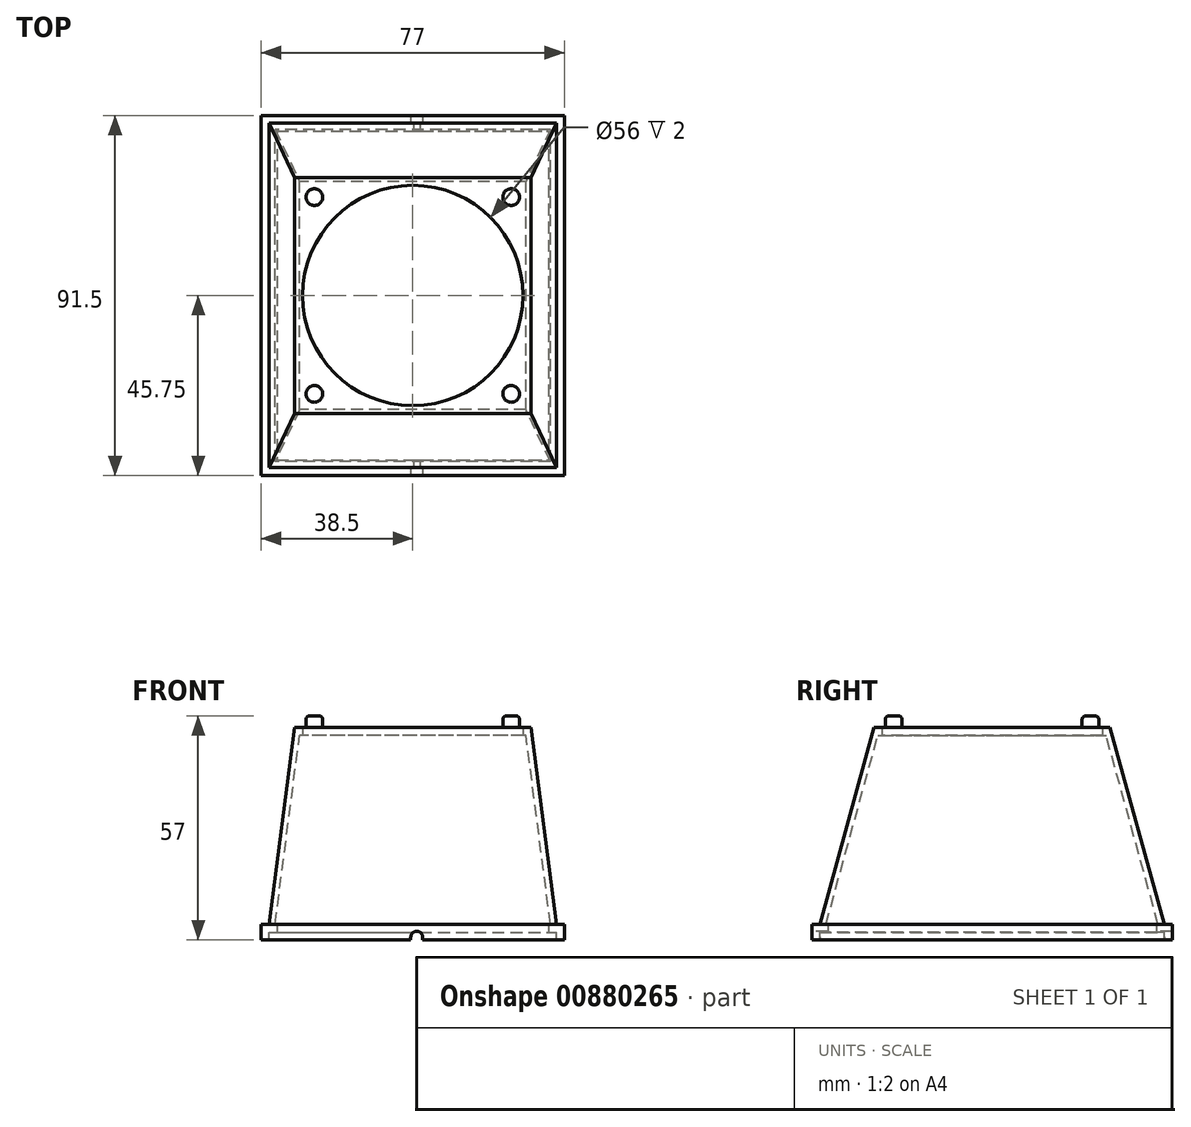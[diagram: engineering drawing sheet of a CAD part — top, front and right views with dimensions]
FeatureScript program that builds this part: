
annotation { "Feature Type Name" : "Feature", "Feature Type Description" : "" }
export const myFeature = defineFeature(function(context is Context, id is Id, definition is map)
    precondition{}
    {
        {
            var Q0;
            Q0=qCreatedBy(makeId("Top.planeOp"),FACE);
            var sketch = newSketch(context, id + "F0", { "sketchPlane" : qUnion([Q0])});
            skCircle(sketch, "E0", {"center": v(0, 0) * mm, "radius": 28 * mm});
            skLineSegment(sketch, "E1.bottom", {"start": v(-30, 30) * mm, "end": v(30, 30) * mm});
            skLineSegment(sketch, "E1.top", {"start": v(-30, -30) * mm, "end": v(30, -30) * mm});
            skLineSegment(sketch, "E1.left", {"start": v(-30, 30) * mm, "end": v(-30, -30) * mm});
            skLineSegment(sketch, "E1.right", {"start": v(30, 30) * mm, "end": v(30, -30) * mm});
            skLineSegment(sketch, "E2.bottom", {"start": v(-34.5, 41.75) * mm, "end": v(34.5, 41.75) * mm});
            skLineSegment(sketch, "E2.top", {"start": v(-34.5, -41.75) * mm, "end": v(34.5, -41.75) * mm});
            skLineSegment(sketch, "E2.left", {"start": v(-34.5, 41.75) * mm, "end": v(-34.5, -41.75) * mm});
            skLineSegment(sketch, "E2.right", {"start": v(34.5, 41.75) * mm, "end": v(34.5, -41.75) * mm});
            skLineSegment(sketch, "E3.bottom", {"start": v(-36.5, -43.75) * mm, "end": v(36.5, -43.75) * mm});
            skLineSegment(sketch, "E3.top", {"start": v(-36.5, 43.75) * mm, "end": v(36.5, 43.75) * mm});
            skLineSegment(sketch, "E3.left", {"start": v(-36.5, -43.75) * mm, "end": v(-36.5, 43.75) * mm});
            skLineSegment(sketch, "E3.right", {"start": v(36.5, -43.75) * mm, "end": v(36.5, 43.75) * mm});
            skLineSegment(sketch, "E4.bottom", {"start": v(-38.5, 45.75) * mm, "end": v(38.5, 45.75) * mm});
            skLineSegment(sketch, "E4.top", {"start": v(-38.5, -45.75) * mm, "end": v(38.5, -45.75) * mm});
            skLineSegment(sketch, "E4.left", {"start": v(-38.5, 45.75) * mm, "end": v(-38.5, -45.75) * mm});
            skLineSegment(sketch, "E4.right", {"start": v(38.5, 45.75) * mm, "end": v(38.5, -45.75) * mm});
            skCircle(sketch, "E5", {"center": v(-25, 25) * mm, "radius": 2.12 * mm});
            skCircle(sketch, "E6.1.0", {"center": v(-25, -25) * mm, "radius": 2.12 * mm});
            skCircle(sketch, "E6.2.0", {"center": v(25, -25) * mm, "radius": 2.12 * mm});
            skCircle(sketch, "E6.3.0", {"center": v(25, 25) * mm, "radius": 2.12 * mm});
            skSolve(sketch);
        }
        {
            var Q0;
            Q0=makeQuery(id+"F0.imprint","IMPRINT",FACE,{"disambiguationData":[TD([[makeQuery(id+"F0.imprint","IMPRINT",EDGE,{"derivedFrom":sQuery(id+"F0.wireOp",EDGE,"E2.bottom")}),1.0]])]});
            extrude(context, id + "F1", {"entities" : qUnion([Q0]), "depth" : 2 * mm, "offsetDistance" : 25 * mm});
        }
        {
            var Q0;
            Q0=makeQuery(id+"F0.imprint","IMPRINT",FACE,{"disambiguationData":[TD([[makeQuery(id+"F0.imprint","IMPRINT",EDGE,{"derivedFrom":sQuery(id+"F0.wireOp",EDGE,"E0")}),-1.0]])]});
            var Q1;
            Q1=makeQuery(id+"F0.imprint","IMPRINT",FACE,{"disambiguationData":[TD([[makeQuery(id+"F0.imprint","IMPRINT",EDGE,{"derivedFrom":sQuery(id+"F0.wireOp",EDGE,"E6.3.0")}),1.0]])]});
            var Q2;
            Q2=makeQuery(id+"F0.imprint","IMPRINT",FACE,{"disambiguationData":[TD([[makeQuery(id+"F0.imprint","IMPRINT",EDGE,{"derivedFrom":sQuery(id+"F0.wireOp",EDGE,"E5")}),1.0]])]});
            var Q3;
            Q3=makeQuery(id+"F0.imprint","IMPRINT",FACE,{"disambiguationData":[TD([[makeQuery(id+"F0.imprint","IMPRINT",EDGE,{"derivedFrom":sQuery(id+"F0.wireOp",EDGE,"E6.1.0")}),1.0]])]});
            var Q4;
            Q4=makeQuery(id+"F0.imprint","IMPRINT",FACE,{"disambiguationData":[TD([[makeQuery(id+"F0.imprint","IMPRINT",EDGE,{"derivedFrom":sQuery(id+"F0.wireOp",EDGE,"E6.2.0")}),1.0]])]});
            extrude(context, id + "F2", {"entities" : qUnion([Q0, Q1, Q2, Q3, Q4]), "operationType" : NewBodyOperationType.ADD, "depth" : 52 * mm, "offsetDistance" : 25 * mm, "hasSecondDirection" : true, "secondDirectionOppositeDirection" : false, "secondDirectionDepth" : 50 * mm});
        }
        {
            var Q0;
            Q0=makeQuery(id+"F2.opExtrude","SWEPT_FACE",FACE,{"disambiguationData":[OSD([sQuery(id+"F0.wireOp",EDGE,"E1.bottom")])]});
            var Q1;
            Q1=makeQuery(id+"F1.opExtrude","SWEPT_FACE",FACE,{"disambiguationData":[OSD([sQuery(id+"F0.wireOp",EDGE,"E3.top")])]});
            loft(context, id + "F3", {"operationType" : NewBodyOperationType.ADD, "sheetProfilesArray" : [{ "sheetProfileEntities" : qUnion([Q0]) }, { "sheetProfileEntities" : qUnion([Q1]) }]});
        }
        {
            var Q0;
            Q0=makeQuery(id+"F2.opExtrude","SWEPT_FACE",FACE,{"disambiguationData":[OSD([sQuery(id+"F0.wireOp",EDGE,"E1.right")])]});
            var Q1;
            Q1=makeQuery(id+"F1.opExtrude","SWEPT_FACE",FACE,{"disambiguationData":[OSD([sQuery(id+"F0.wireOp",EDGE,"E3.right")])]});
            loft(context, id + "F4", {"operationType" : NewBodyOperationType.ADD, "sheetProfilesArray" : [{ "sheetProfileEntities" : qUnion([Q0]) }, { "sheetProfileEntities" : qUnion([Q1]) }]});
        }
        {
            var Q0;
            Q0=makeQuery(id+"F1.opExtrude","SWEPT_FACE",FACE,{"disambiguationData":[OSD([sQuery(id+"F0.wireOp",EDGE,"E3.left")])]});
            var Q1;
            Q1=makeQuery(id+"F2.opExtrude","SWEPT_FACE",FACE,{"disambiguationData":[OSD([sQuery(id+"F0.wireOp",EDGE,"E1.left")])]});
            loft(context, id + "F5", {"operationType" : NewBodyOperationType.ADD, "sheetProfilesArray" : [{ "sheetProfileEntities" : qUnion([Q0]) }, { "sheetProfileEntities" : qUnion([Q1]) }]});
        }
        {
            var Q0;
            Q0=makeQuery(id+"F2.opExtrude","SWEPT_FACE",FACE,{"disambiguationData":[OSD([sQuery(id+"F0.wireOp",EDGE,"E1.top")])]});
            var Q1;
            Q1=makeQuery(id+"F1.opExtrude","SWEPT_FACE",FACE,{"disambiguationData":[OSD([sQuery(id+"F0.wireOp",EDGE,"E3.bottom")])]});
            loft(context, id + "F6", {"operationType" : NewBodyOperationType.ADD, "sheetProfilesArray" : [{ "sheetProfileEntities" : qUnion([Q0]) }, { "sheetProfileEntities" : qUnion([Q1]) }]});
        }
        {
            var Q0;
            Q0=makeQuery(id+"F0.imprint","IMPRINT",FACE,{"disambiguationData":[TD([[makeQuery(id+"F0.imprint","IMPRINT",EDGE,{"derivedFrom":sQuery(id+"F0.wireOp",EDGE,"E3.bottom")}),-1.0]])]});
            extrude(context, id + "F7", {"entities" : qUnion([Q0]), "operationType" : NewBodyOperationType.ADD, "oppositeDirection" : true, "depth" : 2 * mm, "offsetDistance" : 25 * mm, "hasSecondDirection" : true, "secondDirectionOppositeDirection" : false, "secondDirectionDepth" : 2 * mm});
        }
        {
            var Q0;
            Q0=makeQuery(id+"F7.opExtrude","SWEPT_FACE",FACE,{"disambiguationData":[OSD([sQuery(id+"F0.wireOp",EDGE,"E4.top")])]});
            var sketch = newSketch(context, id + "F8", { "sketchPlane" : qUnion([Q0])});
            skArc(sketch, "E7", {"start": v(2.5, -1.25) * mm, "mid": v(1, 0.25) * mm, "end": v(-0.5, -1.25) * mm});
            skLineSegment(sketch, "E8", {"start": v(2.5, -1.25) * mm, "end": v(2.5, -2) * mm});
            skPoint(sketch, "E9.end.orphan", {"position": v(1, -2) * mm});
            skPoint(sketch, "E10.center.orphan", {"position": v(0, -1.25) * mm});
            skPoint(sketch, "E11.start.orphan", {"position": v(-1, -1.25) * mm});
            skLineSegment(sketch, "E12", {"start": v(-0.5, -1.25) * mm, "end": v(-0.5, -2) * mm});
            skSolve(sketch);
        }
        {
            var Q0;
            Q0=makeQuery(id+"F8.imprint","IMPRINT",FACE,{"disambiguationData":[TD([[makeQuery(id+"F8.imprint","IMPRINT",EDGE,{"derivedFrom":sQuery(id+"F8.wireOp",EDGE,"E7")}),1.0]])]});
            extrude(context, id + "F9", {"entities" : qUnion([Q0]), "operationType" : NewBodyOperationType.REMOVE, "endBound" : BoundingType.THROUGH_ALL, "oppositeDirection" : true, "depth" : 25 * mm, "offsetDistance" : 25 * mm});
        }
        {
            var Q0;
            Q0=makeQuery(id+"F0.imprint","IMPRINT",FACE,{"disambiguationData":[TD([[makeQuery(id+"F0.imprint","IMPRINT",EDGE,{"derivedFrom":sQuery(id+"F0.wireOp",EDGE,"E6.3.0")}),1.0]])]});
            var Q1;
            Q1=makeQuery(id+"F0.imprint","IMPRINT",FACE,{"disambiguationData":[TD([[makeQuery(id+"F0.imprint","IMPRINT",EDGE,{"derivedFrom":sQuery(id+"F0.wireOp",EDGE,"E5")}),1.0]])]});
            var Q2;
            Q2=makeQuery(id+"F0.imprint","IMPRINT",FACE,{"disambiguationData":[TD([[makeQuery(id+"F0.imprint","IMPRINT",EDGE,{"derivedFrom":sQuery(id+"F0.wireOp",EDGE,"E6.1.0")}),1.0]])]});
            var Q3;
            Q3=makeQuery(id+"F0.imprint","IMPRINT",FACE,{"disambiguationData":[TD([[makeQuery(id+"F0.imprint","IMPRINT",EDGE,{"derivedFrom":sQuery(id+"F0.wireOp",EDGE,"E6.2.0")}),1.0]])]});
            extrude(context, id + "F10", {"entities" : qUnion([Q0, Q1, Q2, Q3]), "operationType" : NewBodyOperationType.ADD, "depth" : 55 * mm, "offsetDistance" : 25 * mm, "hasSecondDirection" : true, "secondDirectionOppositeDirection" : false, "secondDirectionDepth" : 51 * mm});
        }
        {
            var Q0;
            Q0=makeQuery(id+"F10.opExtrude","CAP_EDGE",EDGE,{"disambiguationData":[OSD([sQuery(id+"F0.wireOp",EDGE,"E6.3.0")])],"isStart":false});
            var Q1;
            Q1=makeQuery(id+"F10.opExtrude","CAP_FACE",FACE,{"disambiguationData":[OSD([sQuery(id+"F0.wireOp",EDGE,"E6.2.0")])],"isStart":false});
            var Q2;
            Q2=makeQuery(id+"F10.opExtrude","CAP_FACE",FACE,{"disambiguationData":[OSD([sQuery(id+"F0.wireOp",EDGE,"E6.1.0")])],"isStart":false});
            var Q3;
            Q3=makeQuery(id+"F10.opExtrude","CAP_EDGE",EDGE,{"disambiguationData":[OSD([sQuery(id+"F0.wireOp",EDGE,"E5")])],"isStart":false});
            var Q4;
            {var subQ0=sQuery(id+"F0.wireOp",EDGE,"E1.right");var subQ1=sQuery(id+"F0.wireOp",EDGE,"E1.bottom");var subQ2=makeQuery(id+"F2.opExtrude","CAP_VERTEX",VERTEX,{"disambiguationData":[OSD([subQ1,subQ0])],"isStart":true});var subQ3=sQuery(id+"F0.wireOp",EDGE,"E1.top");var subQ4=sQuery(id+"F0.wireOp",EDGE,"E3.right");var subQ5=sQuery(id+"F0.wireOp",EDGE,"E3.top");var subQ6=sQuery(id+"F0.wireOp",EDGE,"E3.bottom");Q4=makeQuery(id+"F4.opLoft","SWEPT_FACE",FACE,{"disambiguationData":[OSD([subQ1,subQ3,subQ0,subQ6,subQ5,subQ4]),TDD([makeQuery(id+"F1.opExtrude","CAP_VERTEX",VERTEX,{"disambiguationData":[OSD([subQ6,subQ4])],"isStart":true}),makeQuery(id+"F1.opExtrude","CAP_VERTEX",VERTEX,{"disambiguationData":[OSD([subQ5,subQ4])],"isStart":true}),makeQuery(id+"F1.opExtrude","CAP_EDGE",EDGE,{"disambiguationData":[OSD([subQ4])],"isStart":true}),makeQuery(id+"F2.opExtrude","CAP_VERTEX",VERTEX,{"disambiguationData":[OSD([subQ3,subQ0])],"isStart":true}),makeQuery(id+"F2.opExtrude","CAP_EDGE",EDGE,{"disambiguationData":[OSD([subQ0])],"isStart":true}),makeQuery(id+"F3.boolean.opBoolean","MERGE",VERTEX,{"derivedFrom":[subQ2,makeQuery(id+"F3.opLoft","MID_CAP_VERTEX",VERTEX,{"disambiguationData":[OSD([subQ1,subQ0]),TDD([subQ2])],"capPos":0.0})]})])]});}
            fillet(context, id + "F11", {"entities" : qUnion([Q0, Q1, Q2, Q3, Q4]), "radius" : 1 * mm, "tangentPropagation" : true, "allowEdgeOverflow" : false});
        }
        {
            var Q0;
            {var subQ0=sQuery(id+"F0.wireOp",EDGE,"E1.right");var subQ1=sQuery(id+"F0.wireOp",EDGE,"E1.bottom");var subQ2=makeQuery(id+"F2.opExtrude","CAP_VERTEX",VERTEX,{"disambiguationData":[OSD([subQ1,subQ0])],"isStart":false});var subQ3=sQuery(id+"F0.wireOp",EDGE,"E3.right");var subQ4=sQuery(id+"F0.wireOp",EDGE,"E3.top");var subQ5=makeQuery(id+"F1.opExtrude","CAP_VERTEX",VERTEX,{"disambiguationData":[OSD([subQ4,subQ3])],"isStart":false});var subQ6=sQuery(id+"F0.wireOp",EDGE,"E1.top");var subQ7=sQuery(id+"F0.wireOp",EDGE,"E3.bottom");Q0=makeQuery(id+"F4.opLoft","SWEPT_FACE",FACE,{"disambiguationData":[OSD([subQ1,subQ6,subQ0,subQ7,subQ4,subQ3]),TDD([makeQuery(id+"F1.opExtrude","CAP_VERTEX",VERTEX,{"disambiguationData":[OSD([subQ7,subQ3])],"isStart":false}),makeQuery(id+"F1.opExtrude","CAP_EDGE",EDGE,{"disambiguationData":[OSD([subQ3])],"isStart":false}),makeQuery(id+"F2.opExtrude","CAP_VERTEX",VERTEX,{"disambiguationData":[OSD([subQ6,subQ0])],"isStart":false}),makeQuery(id+"F2.opExtrude","CAP_EDGE",EDGE,{"disambiguationData":[OSD([subQ0])],"isStart":false}),makeQuery(id+"F3.boolean.opBoolean","MERGE",VERTEX,{"derivedFrom":[subQ5,makeQuery(id+"F3.opLoft","MID_CAP_VERTEX",VERTEX,{"disambiguationData":[OSD([subQ4,subQ3]),TDD([subQ5])],"capPos":1.0})]}),makeQuery(id+"F3.boolean.opBoolean","MERGE",VERTEX,{"derivedFrom":[subQ2,makeQuery(id+"F3.opLoft","MID_CAP_VERTEX",VERTEX,{"disambiguationData":[OSD([subQ1,subQ0]),TDD([subQ2])],"capPos":0.0})]})])]});}
            extrude(context, id + "F12", {"entities" : qUnion([Q0]), "operationType" : NewBodyOperationType.ADD, "oppositeDirection" : true, "depth" : 1.5 * mm, "offsetDistance" : 25 * mm});
        }
        {
            var Q0;
            {var subQ0=sQuery(id+"F0.wireOp",EDGE,"E1.left");var subQ1=sQuery(id+"F0.wireOp",EDGE,"E1.top");var subQ2=makeQuery(id+"F2.opExtrude","CAP_VERTEX",VERTEX,{"disambiguationData":[OSD([subQ1,subQ0])],"isStart":false});var subQ3=sQuery(id+"F0.wireOp",EDGE,"E3.left");var subQ4=sQuery(id+"F0.wireOp",EDGE,"E3.bottom");var subQ5=makeQuery(id+"F1.opExtrude","CAP_VERTEX",VERTEX,{"disambiguationData":[OSD([subQ4,subQ3])],"isStart":false});var subQ6=sQuery(id+"F0.wireOp",EDGE,"E1.right");var subQ7=makeQuery(id+"F2.opExtrude","CAP_VERTEX",VERTEX,{"disambiguationData":[OSD([subQ1,subQ6])],"isStart":false});var subQ8=sQuery(id+"F0.wireOp",EDGE,"E3.right");var subQ9=makeQuery(id+"F1.opExtrude","CAP_VERTEX",VERTEX,{"disambiguationData":[OSD([subQ4,subQ8])],"isStart":false});Q0=makeQuery(id+"F6.opLoft","SWEPT_FACE",FACE,{"disambiguationData":[OSD([subQ1,subQ0,subQ6,subQ4,subQ3,subQ8]),TDD([makeQuery(id+"F1.opExtrude","CAP_EDGE",EDGE,{"disambiguationData":[OSD([subQ4])],"isStart":false}),makeQuery(id+"F2.opExtrude","CAP_EDGE",EDGE,{"disambiguationData":[OSD([subQ1])],"isStart":false}),makeQuery(id+"F4.boolean.opBoolean","MERGE",VERTEX,{"derivedFrom":[subQ9,makeQuery(id+"F4.opLoft","MID_CAP_VERTEX",VERTEX,{"disambiguationData":[OSD([subQ4,subQ8]),TDD([subQ9])],"capPos":1.0})]}),makeQuery(id+"F4.boolean.opBoolean","MERGE",VERTEX,{"derivedFrom":[subQ7,makeQuery(id+"F4.opLoft","MID_CAP_VERTEX",VERTEX,{"disambiguationData":[OSD([subQ1,subQ6]),TDD([subQ7])],"capPos":0.0})]}),makeQuery(id+"F5.boolean.opBoolean","MERGE",VERTEX,{"derivedFrom":[subQ5,makeQuery(id+"F5.opLoft","MID_CAP_VERTEX",VERTEX,{"disambiguationData":[OSD([subQ4,subQ3]),TDD([subQ5])],"capPos":0.0})]}),makeQuery(id+"F5.boolean.opBoolean","MERGE",VERTEX,{"derivedFrom":[subQ2,makeQuery(id+"F5.opLoft","MID_CAP_VERTEX",VERTEX,{"disambiguationData":[OSD([subQ1,subQ0]),TDD([subQ2])],"capPos":1.0})]})])]});}
            extrude(context, id + "F13", {"entities" : qUnion([Q0]), "operationType" : NewBodyOperationType.ADD, "oppositeDirection" : true, "depth" : 1.5 * mm, "offsetDistance" : 25 * mm});
        }
        {
            var Q0;
            {var subQ0=sQuery(id+"F0.wireOp",EDGE,"E1.left");var subQ1=sQuery(id+"F0.wireOp",EDGE,"E1.bottom");var subQ2=makeQuery(id+"F2.opExtrude","CAP_VERTEX",VERTEX,{"disambiguationData":[OSD([subQ1,subQ0])],"isStart":false});var subQ3=sQuery(id+"F0.wireOp",EDGE,"E3.left");var subQ4=sQuery(id+"F0.wireOp",EDGE,"E3.top");var subQ5=makeQuery(id+"F1.opExtrude","CAP_VERTEX",VERTEX,{"disambiguationData":[OSD([subQ4,subQ3])],"isStart":false});var subQ6=sQuery(id+"F0.wireOp",EDGE,"E1.top");var subQ7=sQuery(id+"F0.wireOp",EDGE,"E3.bottom");Q0=makeQuery(id+"F5.opLoft","SWEPT_FACE",FACE,{"disambiguationData":[OSD([subQ1,subQ6,subQ0,subQ7,subQ4,subQ3]),TDD([makeQuery(id+"F1.opExtrude","CAP_VERTEX",VERTEX,{"disambiguationData":[OSD([subQ7,subQ3])],"isStart":false}),makeQuery(id+"F1.opExtrude","CAP_EDGE",EDGE,{"disambiguationData":[OSD([subQ3])],"isStart":false}),makeQuery(id+"F2.opExtrude","CAP_VERTEX",VERTEX,{"disambiguationData":[OSD([subQ6,subQ0])],"isStart":false}),makeQuery(id+"F2.opExtrude","CAP_EDGE",EDGE,{"disambiguationData":[OSD([subQ0])],"isStart":false}),makeQuery(id+"F3.boolean.opBoolean","MERGE",VERTEX,{"derivedFrom":[subQ5,makeQuery(id+"F3.opLoft","MID_CAP_VERTEX",VERTEX,{"disambiguationData":[OSD([subQ4,subQ3]),TDD([subQ5])],"capPos":1.0})]}),makeQuery(id+"F3.boolean.opBoolean","MERGE",VERTEX,{"derivedFrom":[subQ2,makeQuery(id+"F3.opLoft","MID_CAP_VERTEX",VERTEX,{"disambiguationData":[OSD([subQ1,subQ0]),TDD([subQ2])],"capPos":0.0})]})])]});}
            extrude(context, id + "F14", {"entities" : qUnion([Q0]), "operationType" : NewBodyOperationType.ADD, "oppositeDirection" : true, "depth" : 1.5 * mm, "offsetDistance" : 25 * mm});
        }
        {
            var Q0;
            {var subQ0=sQuery(id+"F0.wireOp",EDGE,"E1.bottom");var subQ1=sQuery(id+"F0.wireOp",EDGE,"E1.right");var subQ2=sQuery(id+"F0.wireOp",EDGE,"E1.left");var subQ3=sQuery(id+"F0.wireOp",EDGE,"E3.top");var subQ4=sQuery(id+"F0.wireOp",EDGE,"E3.right");var subQ5=sQuery(id+"F0.wireOp",EDGE,"E3.left");Q0=makeQuery(id+"F3.opLoft","SWEPT_FACE",FACE,{"disambiguationData":[OSD([subQ0,subQ2,subQ1,subQ3,subQ5,subQ4]),TDD([makeQuery(id+"F1.opExtrude","CAP_VERTEX",VERTEX,{"disambiguationData":[OSD([subQ3,subQ5])],"isStart":false}),makeQuery(id+"F1.opExtrude","CAP_VERTEX",VERTEX,{"disambiguationData":[OSD([subQ3,subQ4])],"isStart":false}),makeQuery(id+"F1.opExtrude","CAP_EDGE",EDGE,{"disambiguationData":[OSD([subQ3])],"isStart":false}),makeQuery(id+"F2.opExtrude","CAP_VERTEX",VERTEX,{"disambiguationData":[OSD([subQ0,subQ2])],"isStart":false}),makeQuery(id+"F2.opExtrude","CAP_VERTEX",VERTEX,{"disambiguationData":[OSD([subQ0,subQ1])],"isStart":false}),makeQuery(id+"F2.opExtrude","CAP_EDGE",EDGE,{"disambiguationData":[OSD([subQ0])],"isStart":false})])]});}
            extrude(context, id + "F15", {"entities" : qUnion([Q0]), "operationType" : NewBodyOperationType.ADD, "oppositeDirection" : true, "depth" : 1.5 * mm, "offsetDistance" : 25 * mm});
        }
    });
